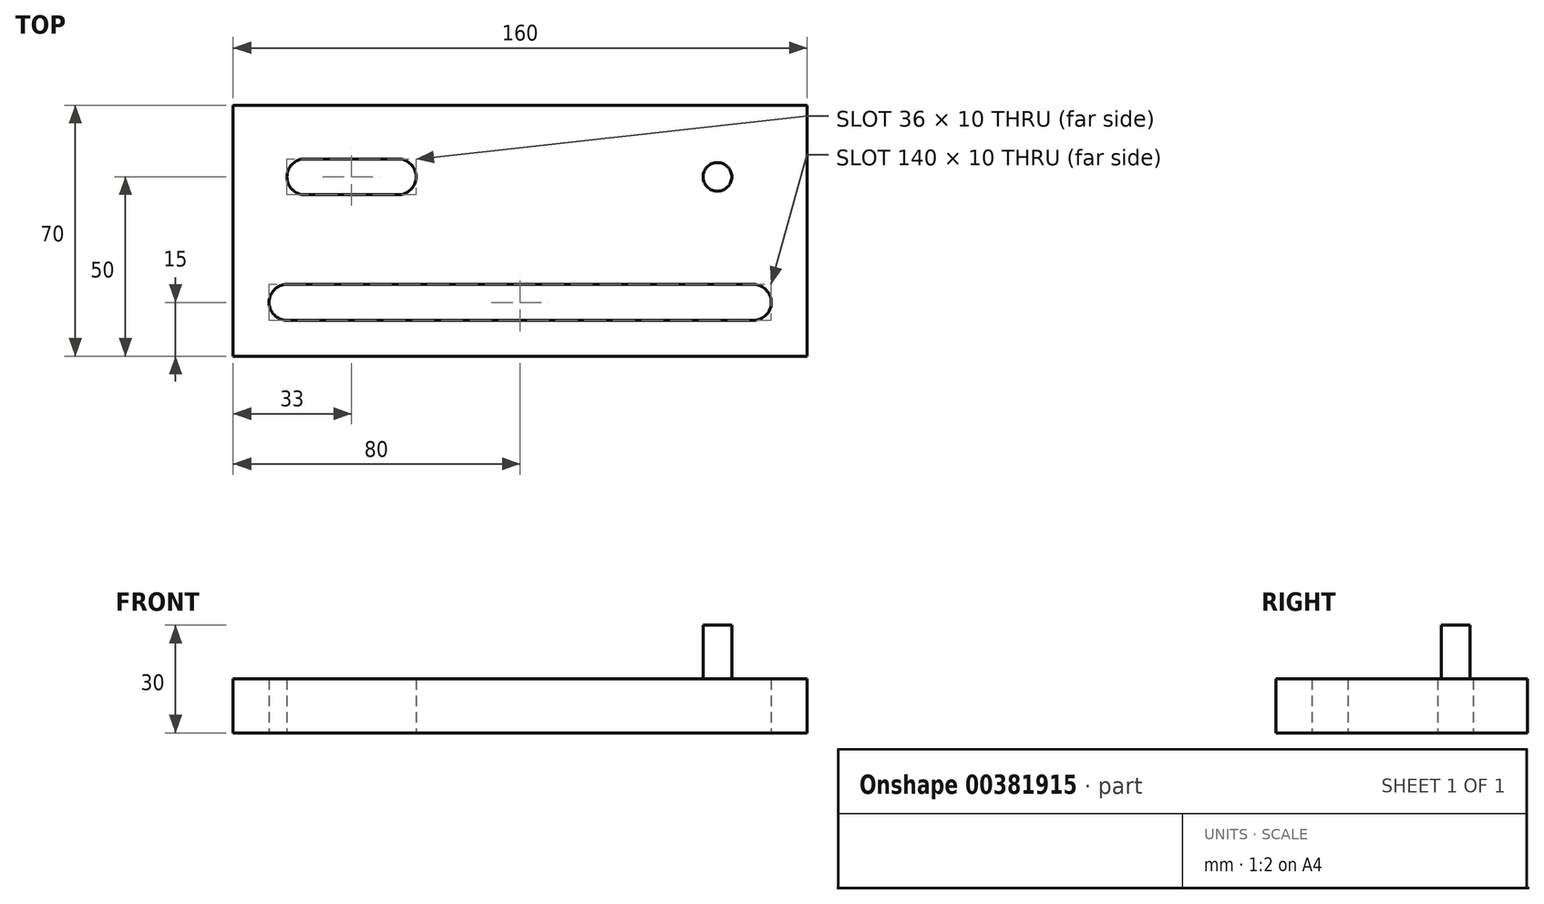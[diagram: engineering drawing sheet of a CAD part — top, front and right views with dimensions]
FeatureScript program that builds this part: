
annotation { "Feature Type Name" : "Feature", "Feature Type Description" : "" }
export const myFeature = defineFeature(function(context is Context, id is Id, definition is map)
    precondition{}
    {
        {
            var Q0;
            Q0=qCreatedBy(makeId("Top.planeOp"),FACE);
            var sketch = newSketch(context, id + "F0", { "sketchPlane" : qUnion([Q0])});
            skLineSegment(sketch, "E0.bottom", {"start": v(0, 0) * mm, "end": v(160, 0) * mm});
            skLineSegment(sketch, "E0.top", {"start": v(0, 70) * mm, "end": v(160, 70) * mm});
            skLineSegment(sketch, "E0.left", {"start": v(0, 0) * mm, "end": v(0, 70) * mm});
            skLineSegment(sketch, "E0.right", {"start": v(160, 0) * mm, "end": v(160, 70) * mm});
            skArc(sketch, "E1", {"start": v(15, 20) * mm, "mid": v(10, 15) * mm, "end": v(15, 10) * mm});
            skLineSegment(sketch, "E2", {"start": v(0, 15) * mm, "end": v(160, 15) * mm, "construction": true});
            skArc(sketch, "E3", {"start": v(145, 10) * mm, "mid": v(150, 15) * mm, "end": v(145, 20) * mm});
            skLineSegment(sketch, "E4", {"start": v(15, 20) * mm, "end": v(145, 20) * mm});
            skLineSegment(sketch, "E5", {"start": v(145, 10) * mm, "end": v(15, 10) * mm});
            skCircle(sketch, "E6", {"center": v(135, 50) * mm, "radius": 4 * mm});
            skCircle(sketch, "E7", {"center": v(135, 50) * mm, "radius": 17.5 * mm, "construction": true});
            skArc(sketch, "E8", {"start": v(20, 55) * mm, "mid": v(15, 50) * mm, "end": v(20, 45) * mm});
            skArc(sketch, "E9", {"start": v(46, 45) * mm, "mid": v(51, 50) * mm, "end": v(46, 55) * mm});
            skLineSegment(sketch, "E10", {"start": v(20, 50) * mm, "end": v(46, 50) * mm, "construction": true});
            skLineSegment(sketch, "E11", {"start": v(20, 55) * mm, "end": v(46, 55) * mm});
            skLineSegment(sketch, "E12", {"start": v(20, 45) * mm, "end": v(46, 45) * mm});
            skCircle(sketch, "E13", {"center": v(148, 50) * mm, "radius": 2.5 * mm, "construction": true});
            skLineSegment(sketch, "E14.bottom", {"start": v(73.5, 62.5) * mm, "end": v(18.5, 62.5) * mm, "construction": true});
            skLineSegment(sketch, "E14.top", {"start": v(73.5, 37.5) * mm, "end": v(18.5, 37.5) * mm, "construction": true});
            skLineSegment(sketch, "E14.left", {"start": v(73.5, 62.5) * mm, "end": v(73.5, 37.5) * mm, "construction": true});
            skLineSegment(sketch, "E14.right", {"start": v(18.5, 62.5) * mm, "end": v(18.5, 37.5) * mm, "construction": true});
            skCircle(sketch, "E15", {"center": v(63, 50) * mm, "radius": 2.5 * mm, "construction": true});
            skSolve(sketch);
        }
        {
            var Q0;
            Q0=makeQuery(id+"F0.imprint","IMPRINT",FACE,{"disambiguationData":[TD([[makeQuery(id+"F0.imprint","IMPRINT",EDGE,{"derivedFrom":sQuery(id+"F0.wireOp",EDGE,"E0.bottom")}),1.0]])]});
            var Q1;
            Q1=makeQuery(id+"F0.imprint","IMPRINT",FACE,{"disambiguationData":[TD([[makeQuery(id+"F0.imprint","IMPRINT",EDGE,{"derivedFrom":sQuery(id+"F0.wireOp",EDGE,"E6")}),1.0]])]});
            extrude(context, id + "F1", {"entities" : qUnion([Q0, Q1]), "depth" : (15) * mm});
        }
        {
            var Q0;
            Q0=makeQuery(id+"F0.imprint","IMPRINT",FACE,{"disambiguationData":[TD([[makeQuery(id+"F0.imprint","IMPRINT",EDGE,{"derivedFrom":sQuery(id+"F0.wireOp",EDGE,"E6")}),1.0]])]});
            extrude(context, id + "F2", {"entities" : qUnion([Q0]), "operationType" : NewBodyOperationType.ADD, "depth" : (30) * mm});
        }
    });
